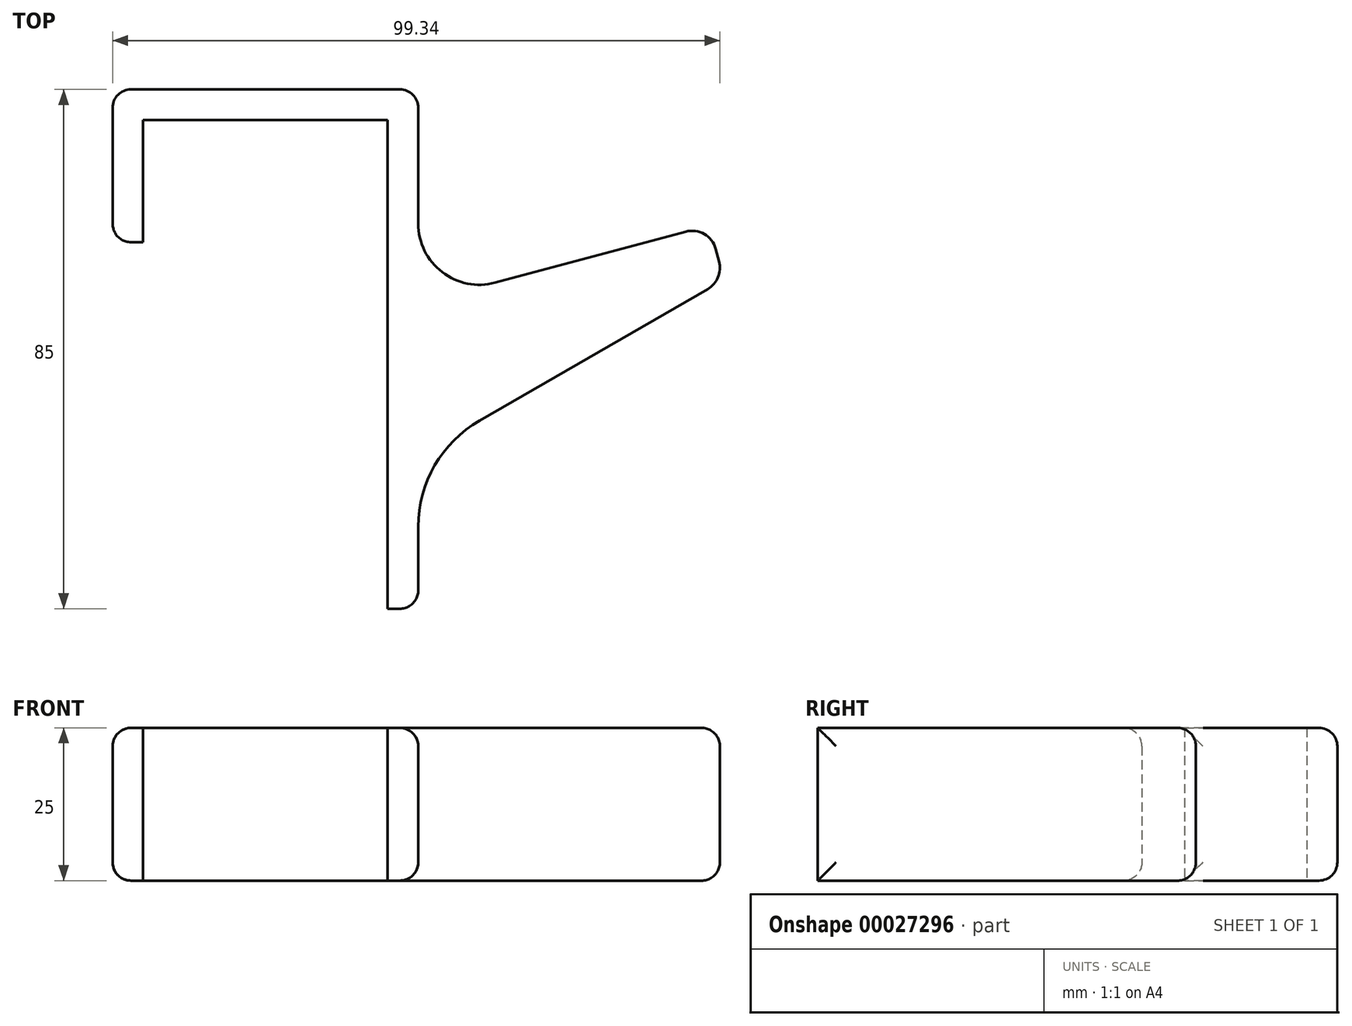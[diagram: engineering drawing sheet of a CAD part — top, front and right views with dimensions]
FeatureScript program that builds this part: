
annotation { "Feature Type Name" : "Feature", "Feature Type Description" : "" }
export const myFeature = defineFeature(function(context is Context, id is Id, definition is map)
    precondition{}
    {
        {
            var Q0;
            Q0=qCreatedBy(makeId("Top.planeOp"),FACE);
            var sketch = newSketch(context, id + "F0", { "sketchPlane" : qUnion([Q0])});
            skLineSegment(sketch, "E0.rect.top", {"start": v(20, 37.5) * mm, "end": v(-20, 37.5) * mm});
            skLineSegment(sketch, "E0.rect.right", {"start": v(-20, 17.5) * mm, "end": v(-20, 37.5) * mm});
            skPoint(sketch, "E0.rect.middle", {"position": v(0, 0) * mm});
            skLineSegment(sketch, "E1.rect.bottom", {"start": v(25, -42.5) * mm, "end": v(20, -42.5) * mm});
            skLineSegment(sketch, "E1.rect.top", {"start": v(22, 42.5) * mm, "end": v(-22, 42.5) * mm});
            skLineSegment(sketch, "E1.rect.left", {"start": v(25, -42.5) * mm, "end": v(25, -29.05) * mm});
            skLineSegment(sketch, "E1.rect.right", {"start": v(-25, 17.5) * mm, "end": v(-25, 39.5) * mm});
            skLineSegment(sketch, "E2", {"start": v(-25, 17.5) * mm, "end": v(-20, 17.5) * mm});
            skLineSegment(sketch, "E3.trimOffspring", {"start": v(25, 20.53) * mm, "end": v(25, 39.5) * mm});
            skLineSegment(sketch, "E4", {"start": v(20, 37.5) * mm, "end": v(20, -42.5) * mm});
            skPoint(sketch, "E5.visualSharp", {"position": v(-25, 42.5) * mm});
            skArc(sketch, "E5.filletArc", {"start": v(-22, 42.5) * mm, "mid": v(-24.12, 41.62) * mm, "end": v(-25, 39.5) * mm});
            skPoint(sketch, "E6.visualSharp", {"position": v(25, 42.5) * mm});
            skArc(sketch, "E6.filletArc", {"start": v(25, 39.5) * mm, "mid": v(24.12, 41.62) * mm, "end": v(22, 42.5) * mm});
            skLineSegment(sketch, "E7", {"start": v(37.59, 10.87) * mm, "end": v(68.75, 19.22) * mm});
            skLineSegment(sketch, "E8", {"start": v(73.65, 16.4) * mm, "end": v(74.2, 14.33) * mm});
            skLineSegment(sketch, "E9", {"start": v(72.34, 9.83) * mm, "end": v(35, -11.73) * mm});
            skPoint(sketch, "E10.visualSharp", {"position": v(25, -17.5) * mm});
            skArc(sketch, "E10.filletArc", {"start": v(35, -11.73) * mm, "mid": v(27.68, -19.05) * mm, "end": v(25, -29.05) * mm});
            skPoint(sketch, "E11.visualSharp", {"position": v(25, 7.5) * mm});
            skArc(sketch, "E11.filletArc", {"start": v(25, 20.53) * mm, "mid": v(28.91, 12.6) * mm, "end": v(37.59, 10.87) * mm});
            skPoint(sketch, "E12.visualSharp", {"position": v(75, 11.37) * mm});
            skArc(sketch, "E12.filletArc", {"start": v(72.34, 9.83) * mm, "mid": v(74.04, 11.77) * mm, "end": v(74.2, 14.33) * mm});
            skPoint(sketch, "E13.visualSharp", {"position": v(72.62, 20.26) * mm});
            skArc(sketch, "E13.filletArc", {"start": v(73.65, 16.4) * mm, "mid": v(71.79, 18.82) * mm, "end": v(68.75, 19.22) * mm});
            skSolve(sketch);
        }
        {
            var Q0;
            Q0 = qSketchRegion(id + "F0", true);
            extrude(context, id + "F1", {"entities" : qUnion([Q0]), "depth" : 25 * mm});
        }
        {
            var Q0;
            Q0=makeQuery(id+"F1.opExtrude","CAP_EDGE",EDGE,{"disambiguationData":[OSD([sQuery(id+"F0.wireOp",EDGE,"E1.rect.top")])],"isStart":false});
            var Q1;
            Q1=makeQuery(id+"F1.opExtrude","CAP_EDGE",EDGE,{"disambiguationData":[OSD([sQuery(id+"F0.wireOp",EDGE,"E1.rect.top")])],"isStart":true});
            var Q2;
            Q2=makeQuery(id+"F1.opExtrude","SWEPT_EDGE",EDGE,{"disambiguationData":[OSD([sQuery(id+"F0.wireOp",EDGE,"E1.rect.right"),sQuery(id+"F0.wireOp",EDGE,"E2")])]});
            var Q3;
            Q3=makeQuery(id+"F1.opExtrude","SWEPT_EDGE",EDGE,{"disambiguationData":[OSD([sQuery(id+"F0.wireOp",EDGE,"E1.rect.bottom"),sQuery(id+"F0.wireOp",EDGE,"E1.rect.left")])]});
            fillet(context, id + "F2", {"entities" : qUnion([Q0, Q1, Q2, Q3]), "radius" : 3 * mm, "tangentPropagation" : true, "allowEdgeOverflow" : false});
        }
    });
